# Revit family: QF_BOURGEAT_Self_GN2_Meuble_neutre_dessus_decaisse
name_source: partatom
category: Equipement spécialisé
revit_build: Autodesk Revit 2015 (Build: 20140606_1530(x64)
units: mm (PartAtom-declared; Revit-internal decimal feet)

## types (7) — shared parameters
Certification = NF alimentaire
Charge max = 150.00 kg
Fabricant = BOURGEAT
Longueur hors tout = 1014 mm  [stored 3.32677 ft]
Nature_isolant = Laine de verre
Poids net à vide = 135.00 kg
Profondeur hors tout = 820 mm
Spécification du Fabricant = Meuble_dessus_decaisse_OASIS
URL catalogue = http://www.bourgeat.fr
lg_etagere = 542 mm  [stored 1.77822 ft]
lg_pare_haleine = 560 mm  [stored 1.83727 ft]
lgconsole = 970 mm  [stored 3.18241 ft]
lgmeuble = 946 mm

## per-type parameters (varying)
| type | Etageres | Hauteur hors tout | Modèle | Pare_haleine | Pieds | Roues |
| GN2_+_pied | Non | 900 mm | 854122 | Non | Oui | Non |
| GN2_+_roues | Non | 900 mm | 854122+854950 | Non | Non | Oui |
| GN2_+_pare_haleine | Non | 1310 mm | 854122+854972 | Oui | Oui | Non |
| GN2_+_etageres | Oui | 900 mm | 854122+854962 | Non | Oui | Non |
| GN2_+_etageres_+_pare_haleine | Oui | 1310 mm | 854122+854962+854972 | Oui | Oui | Non |
| GN2_+_roues_+_etageres | Oui | 900 mm | 854122+854950+854962 | Non | Non | Oui |
| GN2_+_roues_+_etageres_+_pare_haleine | Oui | 1310 mm | 854122+854950+854962+854972 | Oui | Non | Oui |

note: [stored X ft] marks values corroborated as IEEE doubles in the binary element streams (Revit-internal decimal feet)

## geometry (parser evidence)
native form markers: Blend x12
no freeform markers — native parametric forms only
